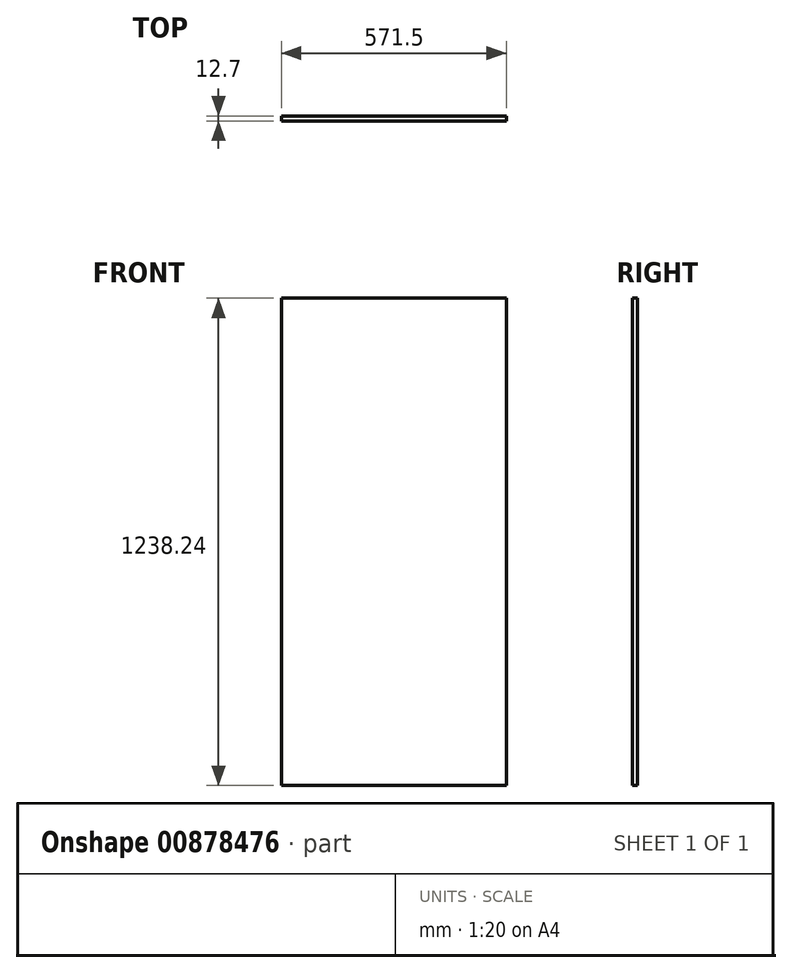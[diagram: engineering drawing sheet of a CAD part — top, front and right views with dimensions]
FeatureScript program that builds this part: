
annotation { "Feature Type Name" : "Feature", "Feature Type Description" : "" }
export const myFeature = defineFeature(function(context is Context, id is Id, definition is map)
    precondition{}
    {
        {
            var Q0;
            Q0=qCreatedBy(makeId("Front.planeOp"),FACE);
            var sketch = newSketch(context, id + "F0", { "sketchPlane" : qUnion([Q0])});
            skLineSegment(sketch, "E0.bottom", {"start": v(-285.75, 619.13) * mm, "end": v(285.75, 619.13) * mm});
            skLineSegment(sketch, "E0.top", {"start": v(-285.75, -619.12) * mm, "end": v(285.75, -619.12) * mm});
            skLineSegment(sketch, "E0.left", {"start": v(-285.75, 619.13) * mm, "end": v(-285.75, -619.13) * mm});
            skLineSegment(sketch, "E0.right", {"start": v(285.75, 619.13) * mm, "end": v(285.75, -619.13) * mm});
            skLineSegment(sketch, "E1", {"start": v(0, 619.12) * mm, "end": v(0, -619.12) * mm, "construction": true});
            skLineSegment(sketch, "E2", {"start": v(-285.75, 0) * mm, "end": v(285.75, 0) * mm, "construction": true});
            skSolve(sketch);
        }
        {
            var Q0;
            Q0 = qSketchRegion(id + "F0", true);
            extrude(context, id + "F1", {"entities" : qUnion([Q0]), "depth" : 12.7 * mm, "offsetDistance" : 25 * mm});
        }
    });
